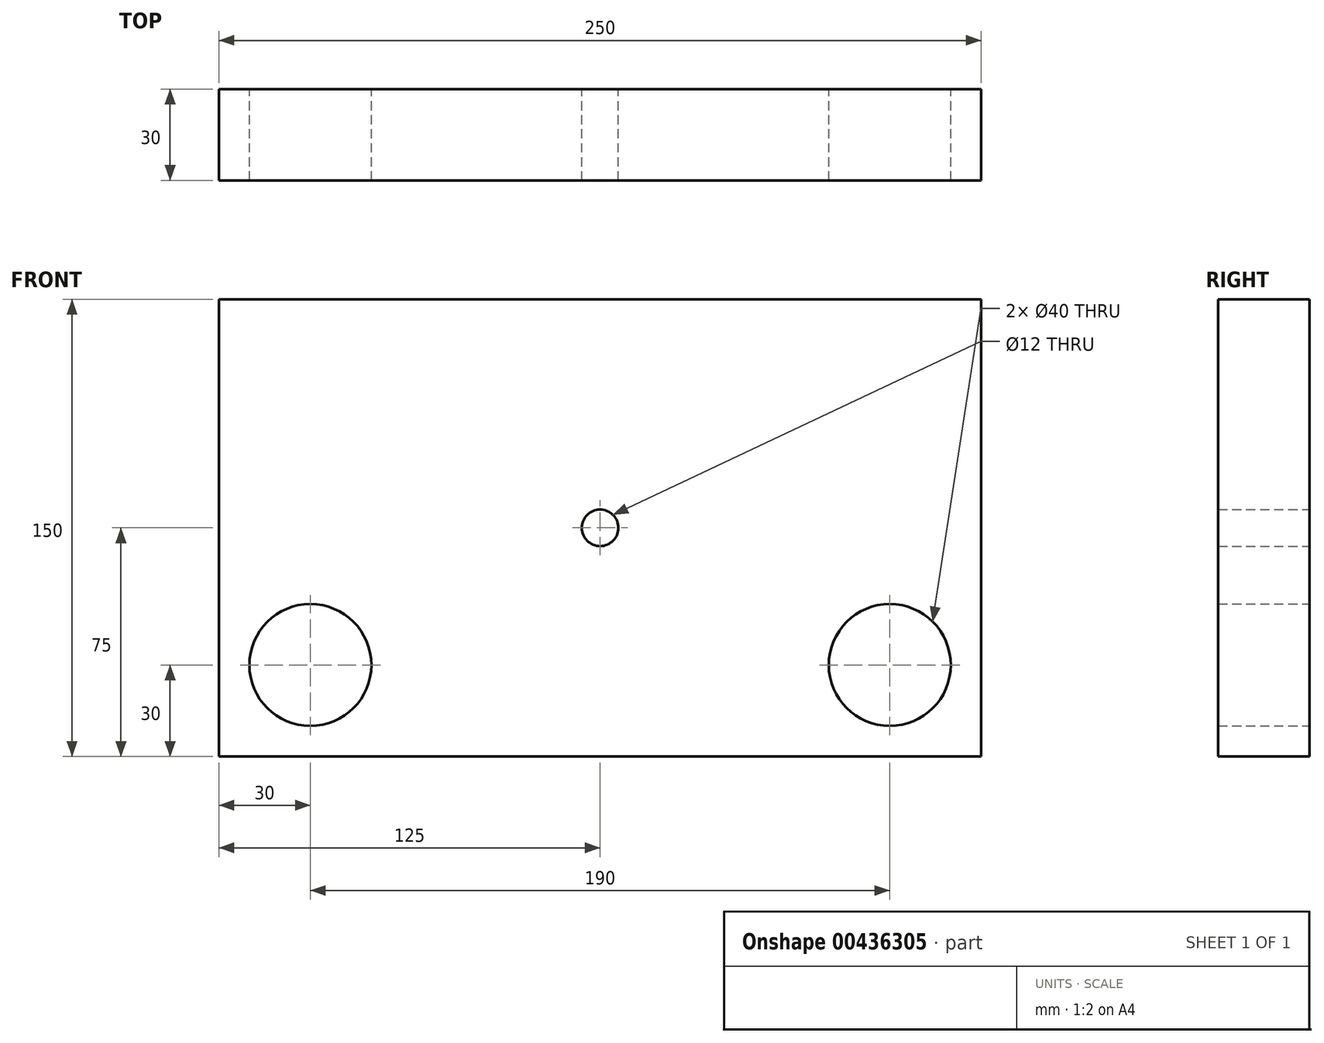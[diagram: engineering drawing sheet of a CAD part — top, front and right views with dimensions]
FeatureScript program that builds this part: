
annotation { "Feature Type Name" : "Feature", "Feature Type Description" : "" }
export const myFeature = defineFeature(function(context is Context, id is Id, definition is map)
    precondition{}
    {
        {
            var Q0;
            Q0=qCreatedBy(makeId("Front.planeOp"),FACE);
            var sketch = newSketch(context, id + "F0", { "sketchPlane" : qUnion([Q0])});
            skLineSegment(sketch, "E0.bottom", {"start": v(125, 75) * mm, "end": v(-125, 75) * mm});
            skLineSegment(sketch, "E0.top", {"start": v(125, -75) * mm, "end": v(-125, -75) * mm});
            skLineSegment(sketch, "E0.left", {"start": v(125, 75) * mm, "end": v(125, -75) * mm});
            skLineSegment(sketch, "E0.right", {"start": v(-125, 75) * mm, "end": v(-125, -75) * mm});
            skPoint(sketch, "E0.middle", {"position": v(0, 0) * mm});
            skCircle(sketch, "E1", {"center": v(-95, -45) * mm, "radius": 20 * mm});
            skCircle(sketch, "E2", {"center": v(95, -45) * mm, "radius": 20 * mm});
            skCircle(sketch, "E3", {"center": v(0, 0) * mm, "radius": 6 * mm});
            skSolve(sketch);
        }
        {
            var Q0;
            Q0 = qSketchRegion(id + "F0", true);
            extrude(context, id + "F1", {"entities" : qUnion([Q0]), "depth" : 30 * mm});
        }
    });
